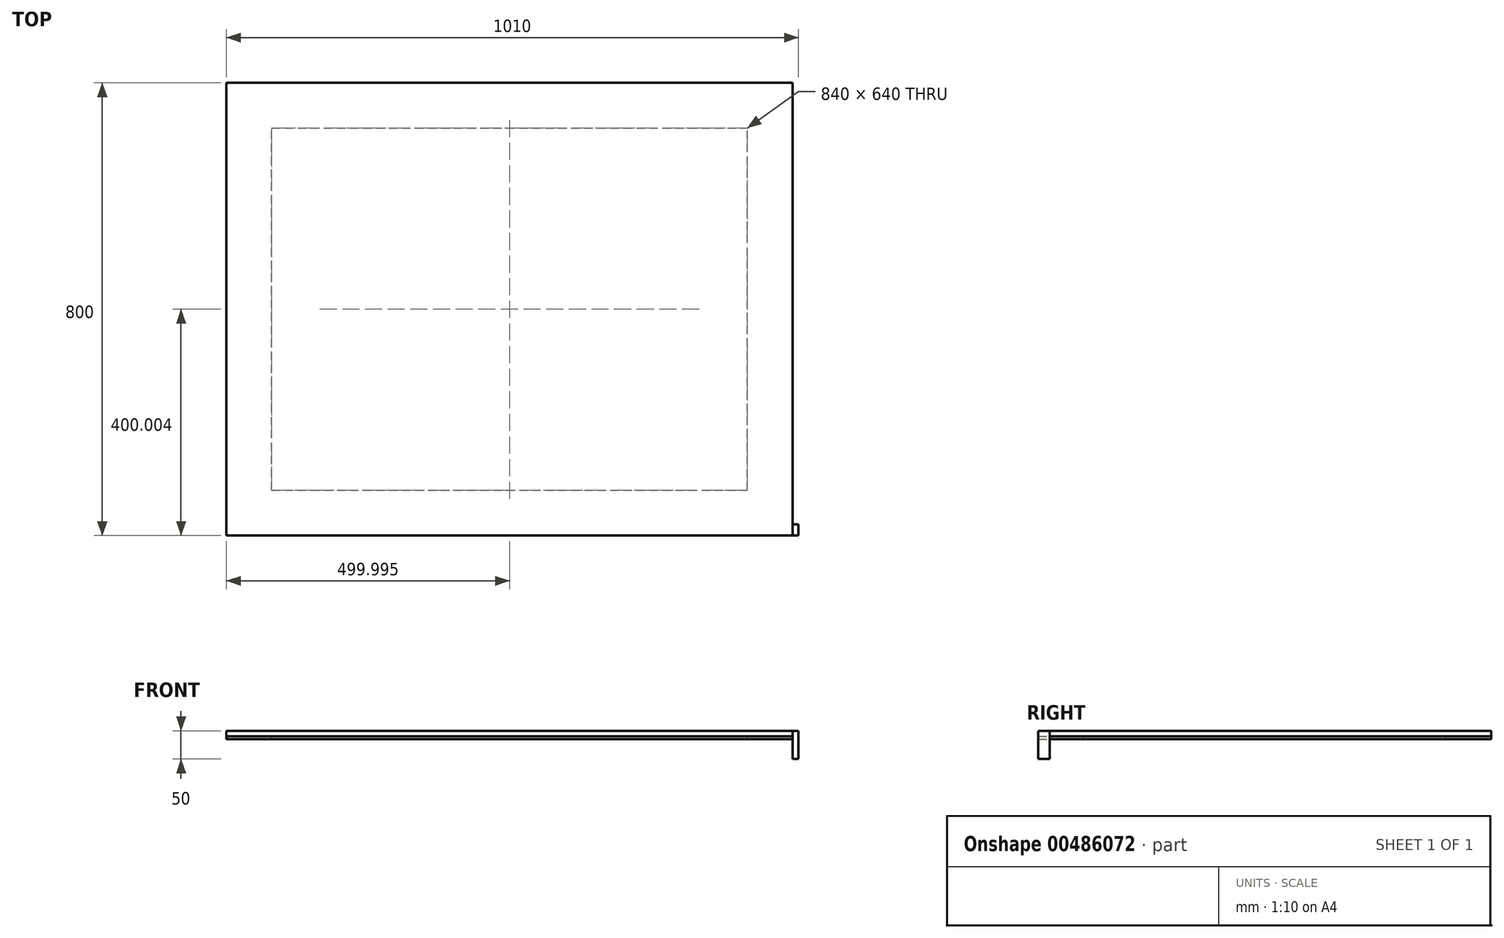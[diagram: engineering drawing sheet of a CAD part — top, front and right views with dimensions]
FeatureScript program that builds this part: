
annotation { "Feature Type Name" : "Feature", "Feature Type Description" : "" }
export const myFeature = defineFeature(function(context is Context, id is Id, definition is map)
    precondition{}
    {
        {
            var Q0;
            Q0=qCreatedBy(makeId("Top.planeOp"),FACE);
            var sketch = newSketch(context, id + "F0", { "sketchPlane" : qUnion([Q0])});
            skLineSegment(sketch, "E0.bottom", {"start": v(-446.06, -309.72) * mm, "end": v(553.94, -309.72) * mm});
            skLineSegment(sketch, "E0.top", {"start": v(-446.06, 490.28) * mm, "end": v(553.94, 490.28) * mm});
            skLineSegment(sketch, "E0.left", {"start": v(-446.06, -309.72) * mm, "end": v(-446.06, 490.28) * mm});
            skLineSegment(sketch, "E0.right", {"start": v(553.94, -309.72) * mm, "end": v(553.94, 490.28) * mm});
            skLineSegment(sketch, "E1.0", {"start": v(-366.06, 410.28) * mm, "end": v(473.94, 410.28) * mm});
            skLineSegment(sketch, "E2.0", {"start": v(-366.06, -309.72) * mm, "end": v(-366.06, 490.28) * mm});
            skLineSegment(sketch, "E3.0", {"start": v(-366.06, -229.72) * mm, "end": v(473.94, -229.72) * mm});
            skLineSegment(sketch, "E4.0", {"start": v(473.94, -309.72) * mm, "end": v(473.94, 490.28) * mm});
            skSolve(sketch);
        }
        {
            var Q0;
            Q0=makeQuery(id+"F0.imprint","IMPRINT",FACE,{"disambiguationData":[TD([[makeQuery(id+"F0.imprint","IMPRINT",EDGE,{"derivedFrom":sQuery(id+"F0.wireOp",EDGE,"E0.bottom")}),1.0]])]});
            var Q1;
            Q1=makeQuery(id+"F0.imprint","IMPRINT",FACE,{"disambiguationData":[TD([[makeQuery(id+"F0.imprint","IMPRINT",EDGE,{"derivedFrom":sQuery(id+"F0.wireOp",EDGE,"DNnGmrQM-lbuE-dcuF-sJEF-m8RkJgQ7nYvQ.bottom")}),1.0]])]});
            var Q2;
            {var subQ4=sQuery(id+"F0.wireOp",EDGE,"E0.left");Q2=makeQuery(id+"F0.imprint","IMPRINT",FACE,{"disambiguationData":[TD([[makeQuery(id+"F0.imprint","IMPRINT",EDGE,{"derivedFrom":subQ4}),-1.0]])]});}
            var Q3;
            {var subQ0=sQuery(id+"F0.wireOp",EDGE,"E1.0");Q3=makeQuery(id+"F0.imprint","IMPRINT",FACE,{"disambiguationData":[TD([[makeQuery(id+"F0.imprint","IMPRINT",EDGE,{"derivedFrom":subQ0}),-1.0]])]});}
            var Q4;
            {var subQ5=sQuery(id+"F0.wireOp",EDGE,"E1.0");Q4=makeQuery(id+"F0.imprint","IMPRINT",FACE,{"disambiguationData":[TD([[makeQuery(id+"F0.imprint","IMPRINT",EDGE,{"derivedFrom":subQ5}),1.0]])]});}
            var Q5;
            {var subQ4=sQuery(id+"F0.wireOp",EDGE,"E0.right");Q5=makeQuery(id+"F0.imprint","IMPRINT",FACE,{"disambiguationData":[TD([[makeQuery(id+"F0.imprint","IMPRINT",EDGE,{"derivedFrom":subQ4}),1.0]])]});}
            extrude(context, id + "F1", {"entities" : qUnion([Q0, Q1, Q2, Q3, Q4, Q5]), "depth" : 10 * mm, "offsetDistance" : 25 * mm});
        }
        {
            var Q0;
            {var subQ4=sQuery(id+"F0.wireOp",EDGE,"E0.left");Q0=makeQuery(id+"F0.imprint","IMPRINT",FACE,{"disambiguationData":[TD([[makeQuery(id+"F0.imprint","IMPRINT",EDGE,{"derivedFrom":subQ4}),-1.0]])]});}
            var Q1;
            {var subQ5=sQuery(id+"F0.wireOp",EDGE,"E1.0");Q1=makeQuery(id+"F0.imprint","IMPRINT",FACE,{"disambiguationData":[TD([[makeQuery(id+"F0.imprint","IMPRINT",EDGE,{"derivedFrom":subQ5}),1.0]])]});}
            var Q2;
            {var subQ5=sQuery(id+"F0.wireOp",EDGE,"E3.0");Q2=makeQuery(id+"F0.imprint","IMPRINT",FACE,{"disambiguationData":[TD([[makeQuery(id+"F0.imprint","IMPRINT",EDGE,{"derivedFrom":subQ5}),-1.0]])]});}
            var Q3;
            {var subQ4=sQuery(id+"F0.wireOp",EDGE,"E0.right");Q3=makeQuery(id+"F0.imprint","IMPRINT",FACE,{"disambiguationData":[TD([[makeQuery(id+"F0.imprint","IMPRINT",EDGE,{"derivedFrom":subQ4}),1.0]])]});}
            extrude(context, id + "F2", {"entities" : qUnion([Q0, Q1, Q2, Q3]), "oppositeDirection" : true, "depth" : 5 * mm, "offsetDistance" : 25 * mm});
        }
        {
            var Q0;
            Q0=makeQuery(id+"F1.opExtrude","SWEPT_FACE",FACE,{"disambiguationData":[OSD([sQuery(id+"F0.wireOp",EDGE,"E0.right")])]});
            var sketch = newSketch(context, id + "F3", { "sketchPlane" : qUnion([Q0])});
            skLineSegment(sketch, "E5.bottom", {"start": v(-309.72, 10) * mm, "end": v(-289.72, 10) * mm});
            skLineSegment(sketch, "E5.top", {"start": v(-309.72, -40) * mm, "end": v(-289.72, -40) * mm});
            skLineSegment(sketch, "E5.left", {"start": v(-309.72, 10) * mm, "end": v(-309.72, -40) * mm});
            skLineSegment(sketch, "E5.right", {"start": v(-289.72, 10) * mm, "end": v(-289.72, -40) * mm});
            skPoint(sketch, "E6", {"position": v(-289.72, -5) * mm});
            skSolve(sketch);
        }
        {
            var Q0;
            Q0 = qSketchRegion(id + "F3", true);
            extrude(context, id + "F4", {"entities" : qUnion([Q0]), "depth" : 10 * mm, "offsetDistance" : 25 * mm});
        }
    });
